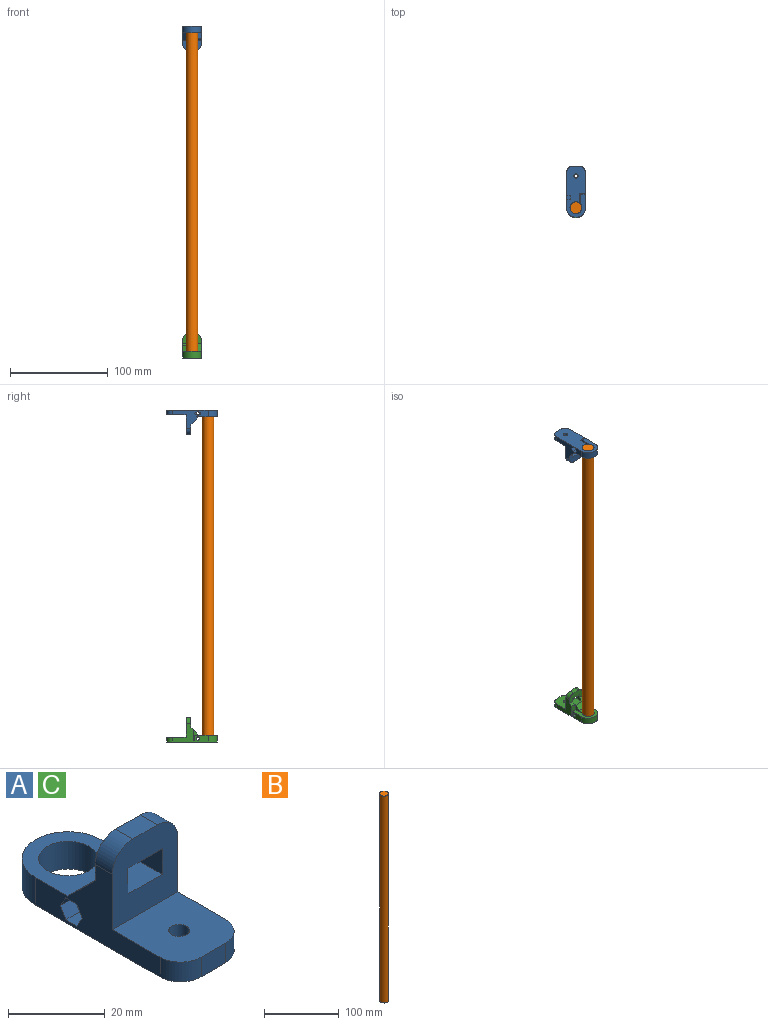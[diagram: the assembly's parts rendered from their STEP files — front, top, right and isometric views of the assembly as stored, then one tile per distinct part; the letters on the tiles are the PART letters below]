
ASSEMBLY  parts=3 mates=2
PART A: 36 faces, bbox 19.2x52.1x25 mm
  f0: plane 12.9x8mm, normal (0,0.71,0.71), area 107.8mm2, adj f2,f6,f14,f18,f27,f30
  f1: plane 20x19.2mm, normal (0,-1,0), area 303.5mm2, adj f4,f13,f14,f17,f27,f28,f29,f30
  f2: plane 19.2x10mm, normal (0,1,0), area 144mm2, adj f0,f4,f13,f14,f28,f29,f30,f33
  f3: cylinder r=1.65mm len=8.9mm, axis (-1,0,0), area 92.3mm2, adj f6,f26
  f4: plane 21.5x19mm, normal (1,0,0), area 199.4mm2, adj f1,f2,f5,f16,f17,f32,f34,f35
  f5: plane 12.5x6.3mm, normal (0,1,0), area 77.5mm2, adj f4,f6,f16,f27,f28,f35
  f6: plane 11.75x9.81mm, normal (1,0,0), area 75mm2, adj f0,f3,f5,f7,f16,f18,f27
  f7: cylinder r=6.15mm len=12.3mm, axis (0,0,-1), area 257.4mm2, adj f6,f8,f16,f18
  f8: plane 9.63x7mm, normal (-1,0,0), area 58.9mm2, adj f7,f9,f16,f18,f19
  f9: plane 7x4.9mm, normal (0,-1,0), area 34.3mm2, adj f8,f10,f16,f18
  f10: plane 13.6x7mm, normal (1,0,0), area 86.6mm2, adj f9,f11,f16,f18,f19
  f11: cylinder r=9.6mm len=19.2mm, axis (0,0,-1), area 211.1mm2, adj f10,f14,f16,f18
  f12: cylinder r=2.15mm len=5mm, axis (0,0,-1), area 67.5mm2, adj f16,f17
  f13: plane 7.2x5mm, normal (0,0,1), area 36mm2, adj f1,f2,f33,f34
  f14: plane 36.5x19mm, normal (-1,0,0), area 292.3mm2, adj f0,f1,f2,f11,f16,f17,f18,f20
  f15: plane 7.2x5mm, normal (0,-1,0), area 36mm2, adj f16,f17,f31,f32
  f16: plane 52.1x19.2mm, normal (0,0,-1), area 790.6mm2, adj f4,f5,f6,f7,f8,f9,f10,f11
  f17: plane 20x19.2mm, normal (0,0,1), area 354mm2, adj f1,f4,f12,f14,f15,f31,f32
  f18: plane 23.2x19.2mm, normal (0,0,1), area 221.6mm2, adj f0,f6,f7,f8,f9,f10,f11,f14
  f19: cylinder r=1.65mm len=4.9mm, axis (-1,0,0), area 50.8mm2, adj f8,f10
  f20: plane 4x3.23mm, normal (0,0,-1), area 12.9mm2, adj f14,f21,f25,f26
  f21: plane 4x2.8mm, normal (0,-0.87,-0.5), area 12.9mm2, adj f14,f20,f22,f26
  f22: plane 4x2.8mm, normal (0,-0.87,0.5), area 12.9mm2, adj f14,f21,f23,f26
  f23: plane 4x3.23mm, normal (0,0,1), area 12.9mm2, adj f14,f22,f24,f26
  f24: plane 4x2.8mm, normal (0,0.87,0.5), area 12.9mm2, adj f14,f23,f25,f26
  f25: plane 4x2.8mm, normal (0,0.87,-0.5), area 12.9mm2, adj f14,f20,f24,f26
  f26: plane 6.47x5.6mm, normal (-1,0,0), area 18.6mm2, adj f3,f20,f21,f22,f23,f24,f25
  f27: plane 10x8.25mm, normal (0,0,1), area 81.2mm2, adj f0,f1,f5,f6,f28,f30
  f28: plane 7.5x6.5mm, normal (-1,0,0), area 37.5mm2, adj f1,f2,f5,f27,f29,f35
  f29: plane 10x5mm, normal (0,0,-1), area 50mm2, adj f1,f2,f28,f30
  f30: plane 8.25x6.5mm, normal (1,0,0), area 37.8mm2, adj f0,f1,f2,f27,f29
  f31: cylinder r=6mm len=6mm, axis (0,0,-1), area 47.1mm2, adj f14,f15,f16,f17
  f32: cylinder r=6mm len=6mm, axis (0,0,-1), area 47.1mm2, adj f4,f15,f16,f17
  f33: cylinder r=6mm len=6mm, axis (0,1,0), area 47.1mm2, adj f1,f2,f13,f14
  f34: cylinder r=6mm len=6mm, axis (0,-1,0), area 47.1mm2, adj f1,f2,f4,f13
  f35: plane 4.6x2.5mm, normal (0,0.71,0.71), area 16.3mm2, adj f2,f4,f5,f28
PART B: 3 faces, bbox 12x12x340 mm
  f0: cylinder r=6mm len=340mm, axis (0,0,-1), area 12817.7mm2, adj f1,f2
  f1: plane 12x12mm, normal (0,0,1), area 113.1mm2, adj f0
  f2: plane 12x12mm, normal (0,0,-1), area 113.1mm2, adj f0
PART C: same geometry as A
PLACE A rot(axis=(1,0,0),180deg) t=(-146.83,-1.7,471.92)mm
PLACE B rot(axis=(0,0,-1),180deg) t=(-178.84,-1.7,131.92)mm
PLACE C rot(axis=(0,0,-1),180deg) t=(-146.83,-1.7,131.92)mm
MATE fastened A.f7 <-> B.f0  axis (0,0,1) through (-146.83,-1.7,471.92)mm
MATE fastened C.f7 <-> B.f0  axis (0,0,-1) through (-146.83,-1.7,131.92)mm
